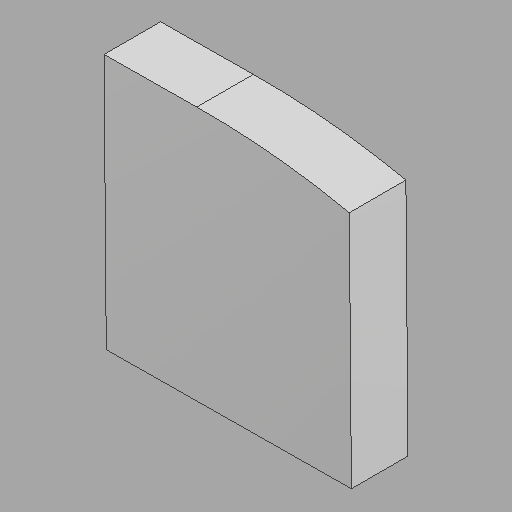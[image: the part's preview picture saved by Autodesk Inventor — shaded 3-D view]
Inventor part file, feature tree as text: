
AUTODESK INVENTOR PART (.ipt)
format: ipt  version: 2022.1 (Build 261234020, 234B)  size: 90,112 bytes
history: imported  units: in
note: dims shown in document units (in); Inventor stores cm internally (conversion verified against a paired STEP export)
features: imported_body x1
ambient origin geometry x8: Origin, YZ Plane, XZ Plane, XY Plane, X Axis, Y Axis, Z Axis, Center Point
bodies: Solid1 (imported_parasolid)
feature tree (1):
  imported_body  NMx_Import_Brep_tag  [imported B-rep: ~7 faces, bbox_mm=[666.359512, 687.953551, 152.4]]
